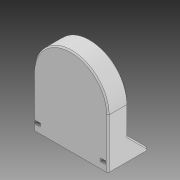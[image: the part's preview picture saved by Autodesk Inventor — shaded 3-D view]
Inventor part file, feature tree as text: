
AUTODESK INVENTOR PART (.ipt)
format: ipt  version: 2020 (Build 240168000, 168)  size: 373,248 bytes
history: native  units: mm
features: extrude x10, sketch x9, fillet x2, chamfer x2, projected_geometry x2, mirror x1, plane x1
ambient origin geometry x8: Origin, YZ Plane, XZ Plane, XY Plane, X Axis, Y Axis, Z Axis, Center Point
bodies: Solid1 (feature_tree)
feature tree (27):
  extrude  "Extrusion1"  Depth=80.0mm
  extrude  "Extrusion2"  Depth=32.5mm
  extrude  "Extrusion3"  Depth=1.0mm
  extrude  "Extrusion7"  Depth=50.0mm TaperAngle=360.0deg
  mirror  "Mirror1"
  extrude  "Extrusion4"  Depth=5.5mm
  plane  "Work Plane1"
  sketch  "Sketch6"  dims[d14=0.0mm d15=0.0mm d16=5.5mm]
  extrude  "Extrusion5"  Depth=7.5mm
  extrude  "Extrusion6"  [1 undecoded]
  fillet  "Fillet1"  Radius=8.2mm
  chamfer  "Chamfer1"  Distance=4.5mm
  fillet  "Fillet2"  Radius=20.75mm
  chamfer  "Chamfer2"  Distance=2.0mm Angle=45.0deg
  extrude  "Extrusion8"  Depth=5.0mm
  extrude  "Extrusion9"  TaperAngle=135.0deg  [1 undecoded]
  extrude  "Extrusion10"  Depth=15.0mm TaperAngle=0.0deg
  sketch  "Sketch1"  dims[d0=95.05mm d2=80.0mm]
  sketch  "Sketch2"  dims[d3=32.5mm d4=0.0mm d5=2.0mm]
  sketch  "Sketch3"  dims[d6=1.0mm d7=0.0mm d8=5.2mm]
  sketch  "Sketch5"  dims[d9=55.0mm d10=50.0mm d12=360.0deg]
  sketch  "Sketch7"  dims[d17=7.5mm d18=7.5mm]
  projected_geometry  "Projected Loop2"
  sketch  "Sketch9"  dims[d20=18.0mm d21=0.0mm d22=-15.0mm d23=8.2mm d24=4.5mm d25=0.0mm d26=20.75mm d27=0.0mm]
  projected_geometry  "Projected Loop4"
  sketch  "Sketch10"  dims[d28=2.0mm d29=2.0mm d30=2.0mm d31=45.0deg]
  sketch  "Sketch11"  dims[d32=30.0mm d33=5.0mm d34=135.0deg d35=15.0mm d36=0.0mm d37=10.0mm d38=5.0mm d39=17.5mm d40=2.0mm d41=2.0mm d42=45.0deg d43=60.0mm d45=52.5mm d46=45.0mm d47=7.5mm d48=0.0mm d49=0.0mm d50=1.0mm d51=0.0mm d52=3.0mm d53=0.0mm]
note: 2 required parameter values undecoded (feature->parameter linkage not recoverable at this tier; creation-order binding heuristic only, values carry confidence <= 0.55)
